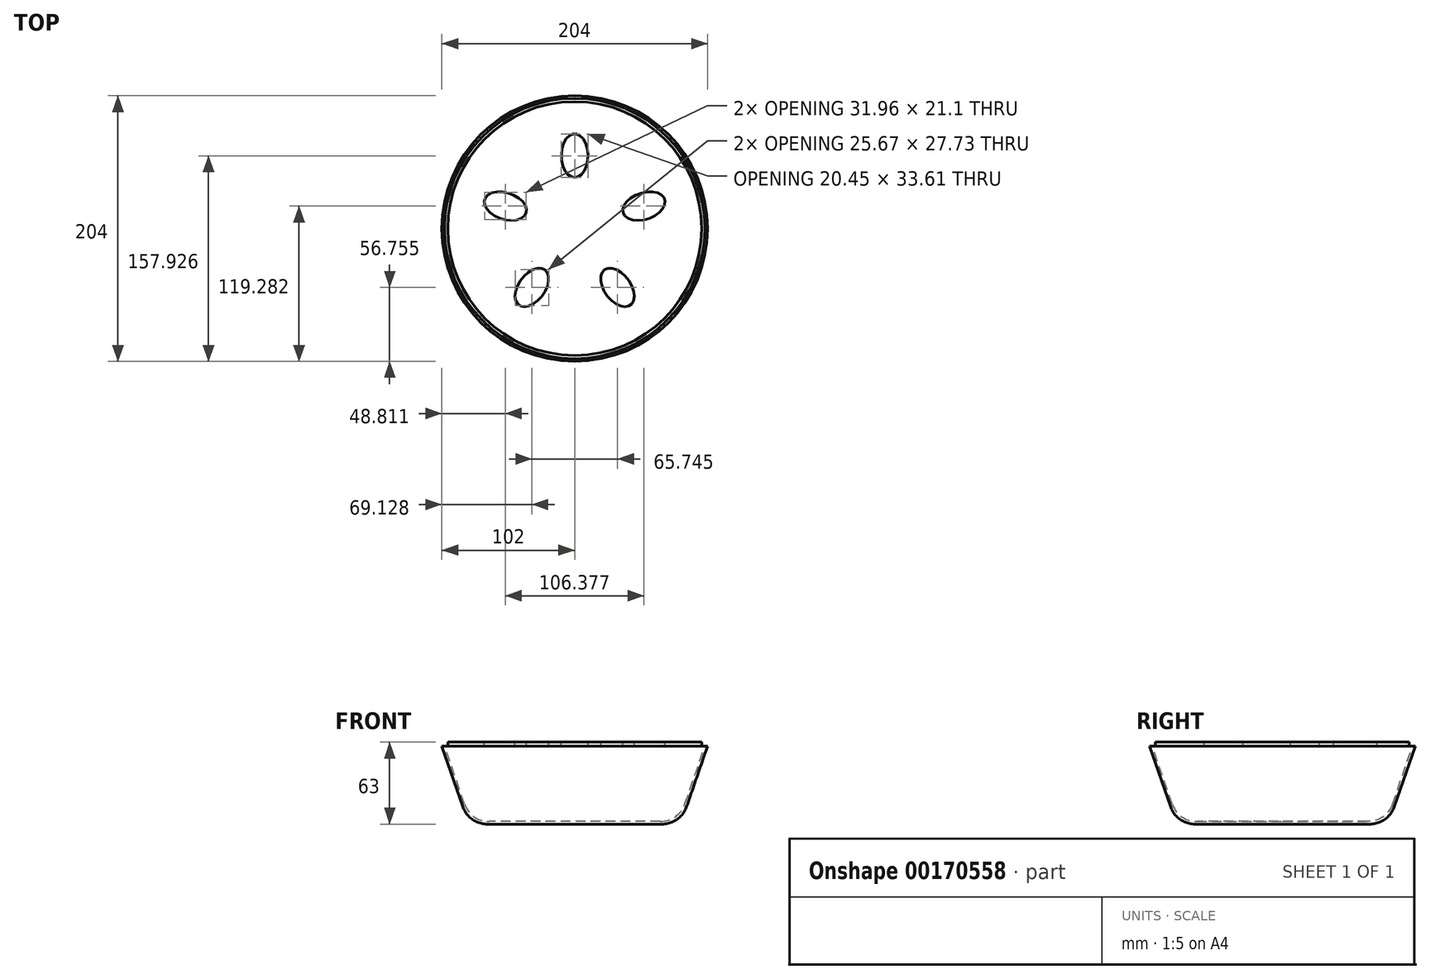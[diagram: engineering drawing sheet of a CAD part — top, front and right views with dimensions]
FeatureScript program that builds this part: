
annotation { "Feature Type Name" : "Feature", "Feature Type Description" : "" }
export const myFeature = defineFeature(function(context is Context, id is Id, definition is map)
    precondition{}
    {
        {
            var Q0;
            Q0=qCreatedBy(makeId("Front.planeOp"),FACE);
            var sketch = newSketch(context, id + "F0", { "sketchPlane" : qUnion([Q0])});
            skLineSegment(sketch, "E0", {"start": v(-102, 60) * mm, "end": v(-85.96, 13.48) * mm});
            skLineSegment(sketch, "E1", {"start": v(-67.05, 0) * mm, "end": v(0, 0) * mm});
            skLineSegment(sketch, "E2", {"start": v(0, 0) * mm, "end": v(0, 2) * mm});
            skLineSegment(sketch, "E3", {"start": v(0, 2) * mm, "end": v(-65.74, 2) * mm});
            skLineSegment(sketch, "E4", {"start": v(-84.65, 15.48) * mm, "end": v(-100, 60) * mm});
            skLineSegment(sketch, "E5", {"start": v(-100, 60) * mm, "end": v(-102, 60) * mm});
            skLineSegment(sketch, "E6", {"start": v(0, 20.64) * mm, "end": v(0, -17.32) * mm, "construction": true});
            skPoint(sketch, "E7.visualSharp", {"position": v(-80, 2) * mm});
            skArc(sketch, "E7.filletArc", {"start": v(-84.65, 15.48) * mm, "mid": v(-77.35, 5.72) * mm, "end": v(-65.74, 2) * mm});
            skPoint(sketch, "E8.visualSharp", {"position": v(-81.31, 0) * mm});
            skArc(sketch, "E8.filletArc", {"start": v(-85.96, 13.48) * mm, "mid": v(-78.66, 3.72) * mm, "end": v(-67.05, 0) * mm});
            skSolve(sketch);
        }
        {
            var Q0;
            Q0=makeQuery(id+"F0.imprint","IMPRINT",FACE,{"disambiguationData":[TD([[makeQuery(id+"F0.imprint","IMPRINT",EDGE,{"derivedFrom":sQuery(id+"F0.wireOp",EDGE,"E0")}),1.0]])]});
            var Q1;
            Q1=sQuery(id+"F0.wireOp",EDGE,"E6");
            revolve(context, id + "F1", {"entities" : qUnion([Q0]), "axis" : qUnion([Q1]), "revolveType" : RevolveType.FULL});
        }
        {
            var Q0;
            Q0=makeQuery(id+"F1.opRevolve","SWEPT_FACE",FACE,{"disambiguationData":[OSD([sQuery(id+"F0.wireOp",EDGE,"E5")])]});
            var sketch = newSketch(context, id + "F2", { "sketchPlane" : qUnion([Q0])});
            skCircle(sketch, "E9", {"center": v(0, 0) * mm, "radius": 97.5 * mm});
            skSolve(sketch);
        }
        {
            var Q0;
            Q0 = qSketchRegion(id + "F2", true);
            extrude(context, id + "F3", {"entities" : qUnion([Q0]), "depth" : 3 * mm});
        }
        {
            var Q0;
            Q0=makeQuery(id+"F3.opExtrude","CAP_FACE",FACE,{"disambiguationData":[OSD([sQuery(id+"F2.wireOp",EDGE,"E9")])],"isStart":false});
            var sketch = newSketch(context, id + "F4", { "sketchPlane" : qUnion([Q0])});
            skEllipse(sketch, "E10", {"center": v(0, 55) * mm, "majorRadius": 40 * mm, "minorRadius": 22.5 * mm, "majorAxis": v(0, -1)});
            skEllipse(sketch, "E11.1.0", {"center": v(-52.3, 17) * mm, "majorRadius": 40 * mm, "minorRadius": 22.5 * mm, "majorAxis": v(0.95, -0.3)});
            skEllipse(sketch, "E11.2.0", {"center": v(-32.33, -44.5) * mm, "majorRadius": 40 * mm, "minorRadius": 22.5 * mm, "majorAxis": v(0.59, 0.8)});
            skEllipse(sketch, "E11.3.0", {"center": v(32.33, -44.5) * mm, "majorRadius": 40 * mm, "minorRadius": 22.5 * mm, "majorAxis": v(-0.59, 0.8)});
            skEllipse(sketch, "E11.4.0", {"center": v(52.3, 17) * mm, "majorRadius": 40 * mm, "minorRadius": 22.5 * mm, "majorAxis": v(-0.95, -0.3)});
            skPoint(sketch, "E11.center", {"position": v(0, 0) * mm});
            skSolve(sketch);
        }
        {
            var Q0;
            Q0=makeQuery(id+"F4.imprint","IMPRINT",FACE,{"disambiguationData":[TD([[makeQuery(id+"F4.imprint","IMPRINT",EDGE,{"derivedFrom":sQuery(id+"F4.wireOp",EDGE,"E10")}),-1.0]])]});
            var sketch = newSketch(context, id + "F5", { "sketchPlane" : qUnion([Q0])});
            skEllipse(sketch, "E12", {"center": v(0, 55.93) * mm, "majorRadius": 16.8 * mm, "minorRadius": 10.23 * mm, "majorAxis": v(0, -1)});
            skEllipse(sketch, "E13.1.0", {"center": v(-53.19, 17.28) * mm, "majorRadius": 16.8 * mm, "minorRadius": 10.23 * mm, "majorAxis": v(0.95, -0.3)});
            skEllipse(sketch, "E13.2.0", {"center": v(-32.87, -45.24) * mm, "majorRadius": 16.8 * mm, "minorRadius": 10.23 * mm, "majorAxis": v(0.59, 0.8)});
            skEllipse(sketch, "E13.3.0", {"center": v(32.87, -45.24) * mm, "majorRadius": 16.8 * mm, "minorRadius": 10.23 * mm, "majorAxis": v(-0.59, 0.8)});
            skEllipse(sketch, "E13.4.0", {"center": v(53.19, 17.28) * mm, "majorRadius": 16.8 * mm, "minorRadius": 10.23 * mm, "majorAxis": v(-0.95, -0.3)});
            skPoint(sketch, "E13.center", {"position": v(0, 0) * mm});
            skSolve(sketch);
        }
        {
            var Q0;
            Q0 = qSketchRegion(id + "F5", true);
            extrude(context, id + "F6", {"entities" : qUnion([Q0]), "operationType" : NewBodyOperationType.REMOVE, "endBound" : BoundingType.UP_TO_NEXT, "oppositeDirection" : true, "depth" : 25 * mm});
        }
    });
